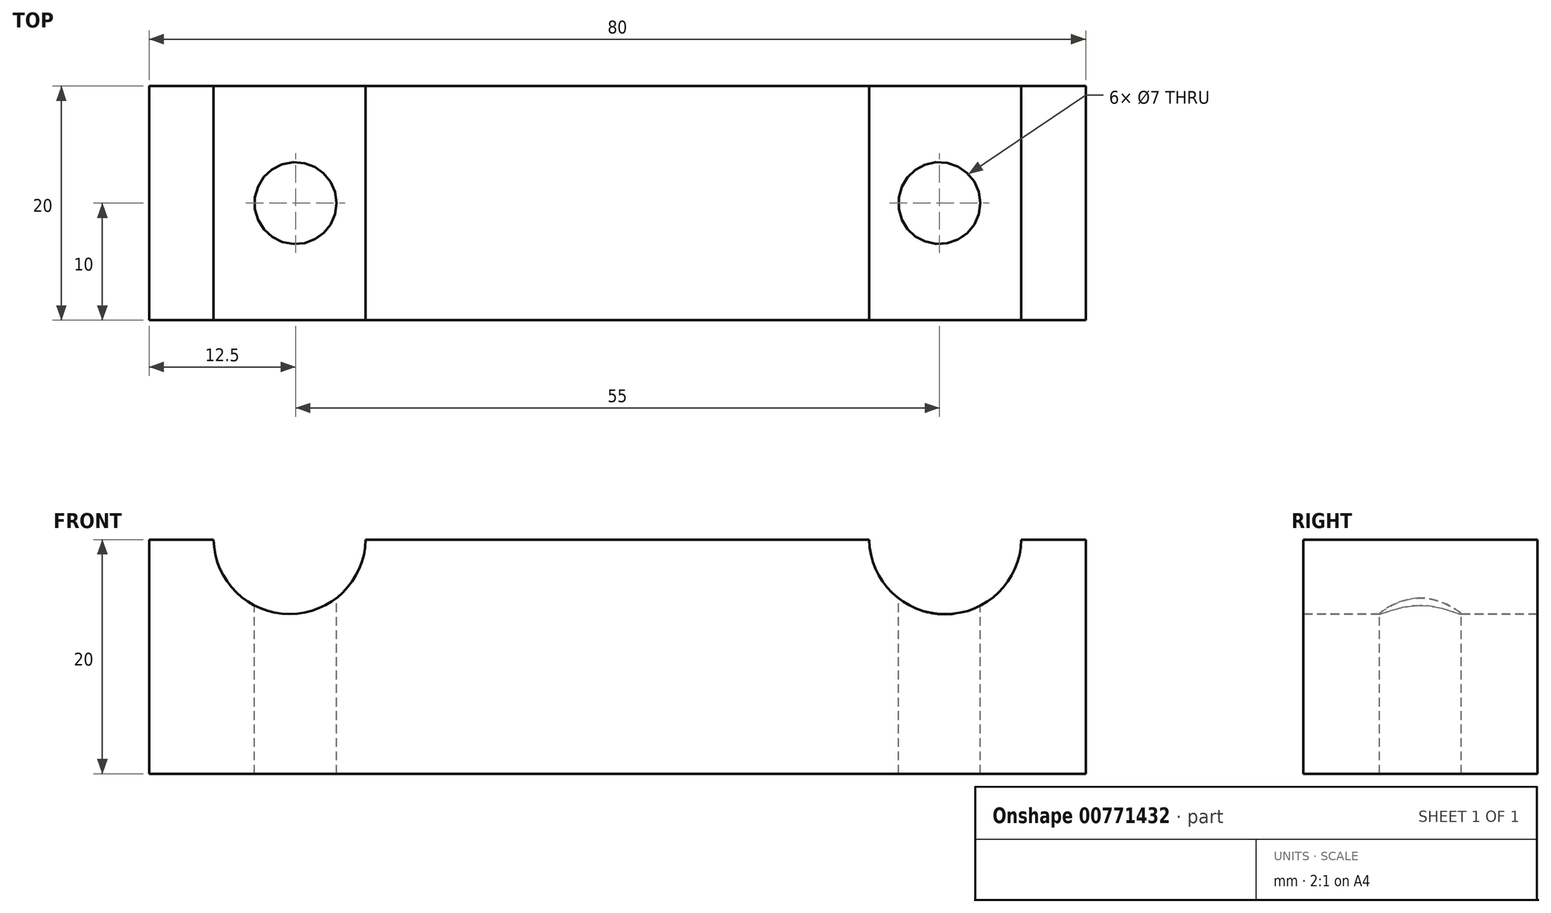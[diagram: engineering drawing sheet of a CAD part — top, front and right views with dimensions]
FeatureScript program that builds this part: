
annotation { "Feature Type Name" : "Feature", "Feature Type Description" : "" }
export const myFeature = defineFeature(function(context is Context, id is Id, definition is map)
    precondition{}
    {
        {
            var Q0;
            Q0=qCreatedBy(makeId("Front.planeOp"),FACE);
            var sketch = newSketch(context, id + "F0", { "sketchPlane" : qUnion([Q0])});
            skLineSegment(sketch, "E0.bottom", {"start": v(-40, 10) * mm, "end": v(40, 10) * mm});
            skLineSegment(sketch, "E0.top", {"start": v(-40, -10) * mm, "end": v(40, -10) * mm});
            skLineSegment(sketch, "E0.left", {"start": v(-40, 10) * mm, "end": v(-40, -10) * mm});
            skLineSegment(sketch, "E0.right", {"start": v(40, 10) * mm, "end": v(40, -10) * mm});
            skPoint(sketch, "E0.middle", {"position": v(0, 0) * mm});
            skSolve(sketch);
        }
        {
            var Q0;
            Q0=qCreatedBy(makeId("Front.planeOp"),FACE);
            var sketch = newSketch(context, id + "F1", { "sketchPlane" : qUnion([Q0])});
            skCircle(sketch, "E1", {"center": v(-28, 10.14) * mm, "radius": 6.5 * mm});
            skCircle(sketch, "E2", {"center": v(28, 10.12) * mm, "radius": 6.5 * mm});
            skSolve(sketch);
        }
        {
            var Q0;
            Q0 = qSketchRegion(id + "F0", true);
            extrude(context, id + "F2", {"entities" : qUnion([Q0]), "endBound" : BoundingType.SYMMETRIC, "depth" : 20 * mm, "offsetDistance" : 25.4 * mm});
        }
        {
            var Q0;
            Q0 = qSketchRegion(id + "F1", true);
            extrude(context, id + "F3", {"entities" : qUnion([Q0]), "operationType" : NewBodyOperationType.REMOVE, "endBound" : BoundingType.SYMMETRIC, "oppositeDirection" : true, "depth" : 20 * mm, "offsetDistance" : 25.4 * mm});
        }
        {
            var Q0;
            Q0=qCreatedBy(makeId("Top.planeOp"),FACE);
            var sketch = newSketch(context, id + "F4", { "sketchPlane" : qUnion([Q0])});
            skCircle(sketch, "E3", {"center": v(-27.5, 0) * mm, "radius": 3.5 * mm});
            skCircle(sketch, "E4", {"center": v(27.5, 0) * mm, "radius": 3.5 * mm});
            skSolve(sketch);
        }
        {
            var Q0;
            Q0 = qSketchRegion(id + "F4", true);
            extrude(context, id + "F5", {"entities" : qUnion([Q0]), "operationType" : NewBodyOperationType.REMOVE, "endBound" : BoundingType.SYMMETRIC, "oppositeDirection" : true, "depth" : 40 * mm, "offsetDistance" : 25.4 * mm});
        }
    });
